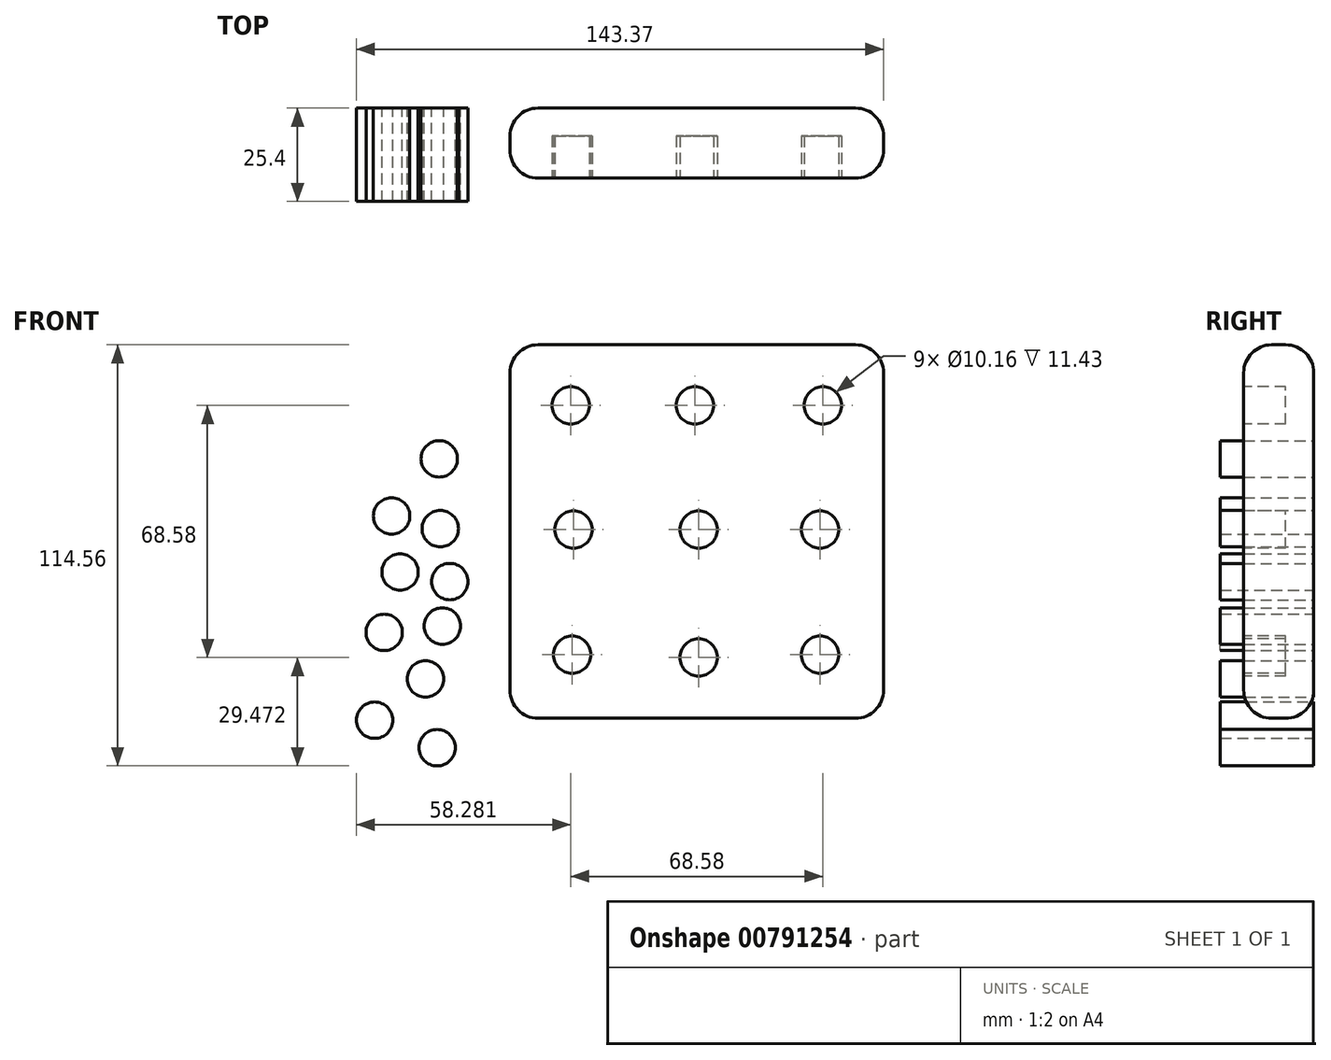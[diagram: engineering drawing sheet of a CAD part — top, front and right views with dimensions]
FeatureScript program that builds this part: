
annotation { "Feature Type Name" : "Feature", "Feature Type Description" : "" }
export const myFeature = defineFeature(function(context is Context, id is Id, definition is map)
    precondition{}
    {
        {
            var Q0;
            Q0=qCreatedBy(makeId("Front.planeOp"),FACE);
            var sketch = newSketch(context, id + "F0", { "sketchPlane" : qUnion([Q0])});
            skLineSegment(sketch, "E0.bottom", {"start": v(70.64, 69.17) * mm, "end": v(-30.96, 69.17) * mm});
            skLineSegment(sketch, "E0.top", {"start": v(70.64, -32.43) * mm, "end": v(-30.96, -32.43) * mm});
            skLineSegment(sketch, "E0.left", {"start": v(70.64, 69.17) * mm, "end": v(70.64, -32.43) * mm});
            skLineSegment(sketch, "E0.right", {"start": v(-30.96, 69.17) * mm, "end": v(-30.96, -32.43) * mm});
            skSolve(sketch);
        }
        {
            var Q0;
            Q0 = qSketchRegion(id + "F0", true);
            extrude(context, id + "F1", {"entities" : qUnion([Q0]), "depth" : 19.05 * mm, "offsetDistance" : 25.4 * mm});
        }
        {
            var Q0;
            Q0=makeQuery(id+"F1.opExtrude","CAP_FACE",FACE,{"disambiguationData":[OSD([sQuery(id+"F0.wireOp",EDGE,"E0.bottom"),sQuery(id+"F0.wireOp",EDGE,"E0.top"),sQuery(id+"F0.wireOp",EDGE,"E0.left"),sQuery(id+"F0.wireOp",EDGE,"E0.right")])],"isStart":false});
            var sketch = newSketch(context, id + "F2", { "sketchPlane" : qUnion([Q0])});
            skPoint(sketch, "E1.centerSnap0", {"position": v(-14.07, 1.35) * mm});
            skCircle(sketch, "E2", {"center": v(-14.45, 52.66) * mm, "radius": 5.08 * mm});
            skCircle(sketch, "E3", {"center": v(19.33, 52.66) * mm, "radius": 5.08 * mm});
            skCircle(sketch, "E4", {"center": v(54.13, 52.66) * mm, "radius": 5.08 * mm});
            skCircle(sketch, "E5", {"center": v(53.37, 18.88) * mm, "radius": 5.08 * mm});
            skCircle(sketch, "E6", {"center": v(20.35, 18.88) * mm, "radius": 5.08 * mm});
            skCircle(sketch, "E7", {"center": v(-13.69, 18.88) * mm, "radius": 5.08 * mm});
            skCircle(sketch, "E8", {"center": v(-14.07, -15.16) * mm, "radius": 5.08 * mm});
            skCircle(sketch, "E9", {"center": v(20.35, -15.92) * mm, "radius": 5.08 * mm});
            skCircle(sketch, "E10", {"center": v(53.37, -15.16) * mm, "radius": 5.08 * mm});
            skSolve(sketch);
        }
        {
            var Q0;
            Q0 = qSketchRegion(id + "F2", true);
            extrude(context, id + "F3", {"entities" : qUnion([Q0]), "operationType" : NewBodyOperationType.REMOVE, "oppositeDirection" : true, "depth" : 11.43 * mm, "offsetDistance" : 25.4 * mm});
        }
        {
            var Q0;
            Q0=qCreatedBy(makeId("Front.planeOp"),FACE);
            var sketch = newSketch(context, id + "F4", { "sketchPlane" : qUnion([Q0])});
            skCircle(sketch, "E11", {"center": v(-50.22, 38.13) * mm, "radius": 4.95 * mm});
            skCircle(sketch, "E12", {"center": v(-63.17, 22.6) * mm, "radius": 4.95 * mm});
            skCircle(sketch, "E13", {"center": v(-60.87, 7.34) * mm, "radius": 4.95 * mm});
            skCircle(sketch, "E14", {"center": v(-49.93, 19.14) * mm, "radius": 4.95 * mm});
            skCircle(sketch, "E15", {"center": v(-47.34, 4.75) * mm, "radius": 4.95 * mm});
            skCircle(sketch, "E16", {"center": v(-65.19, -9.07) * mm, "radius": 4.95 * mm});
            skCircle(sketch, "E17", {"center": v(-49.36, -7.34) * mm, "radius": 4.95 * mm});
            skCircle(sketch, "E18", {"center": v(-53.96, -21.73) * mm, "radius": 4.95 * mm});
            skCircle(sketch, "E19", {"center": v(-50.8, -40.44) * mm, "radius": 4.95 * mm});
            skCircle(sketch, "E20", {"center": v(-67.78, -32.95) * mm, "radius": 4.95 * mm});
            skSolve(sketch);
        }
        {
            var Q0;
            Q0 = qSketchRegion(id + "F4", true);
            extrude(context, id + "F5", {"entities" : qUnion([Q0]), "depth" : 25.4 * mm, "offsetDistance" : 25.4 * mm});
        }
        {
            var Q0;
            Q0=makeQuery(id+"F1.opExtrude","SWEPT_FACE",FACE,{"disambiguationData":[OSD([sQuery(id+"F0.wireOp",EDGE,"E0.left")])]});
            var Q1;
            Q1=makeQuery(id+"F1.opExtrude","SWEPT_FACE",FACE,{"disambiguationData":[OSD([sQuery(id+"F0.wireOp",EDGE,"E0.bottom")])]});
            var Q2;
            Q2=makeQuery(id+"F1.opExtrude","SWEPT_FACE",FACE,{"disambiguationData":[OSD([sQuery(id+"F0.wireOp",EDGE,"E0.right")])]});
            var Q3;
            Q3=makeQuery(id+"F1.opExtrude","SWEPT_FACE",FACE,{"disambiguationData":[OSD([sQuery(id+"F0.wireOp",EDGE,"E0.top")])]});
            fillet(context, id + "F6", {"entities" : qUnion([Q0, Q1, Q2, Q3]), "radius" : 7.62 * mm, "tangentPropagation" : true, "allowEdgeOverflow" : false});
        }
    });
